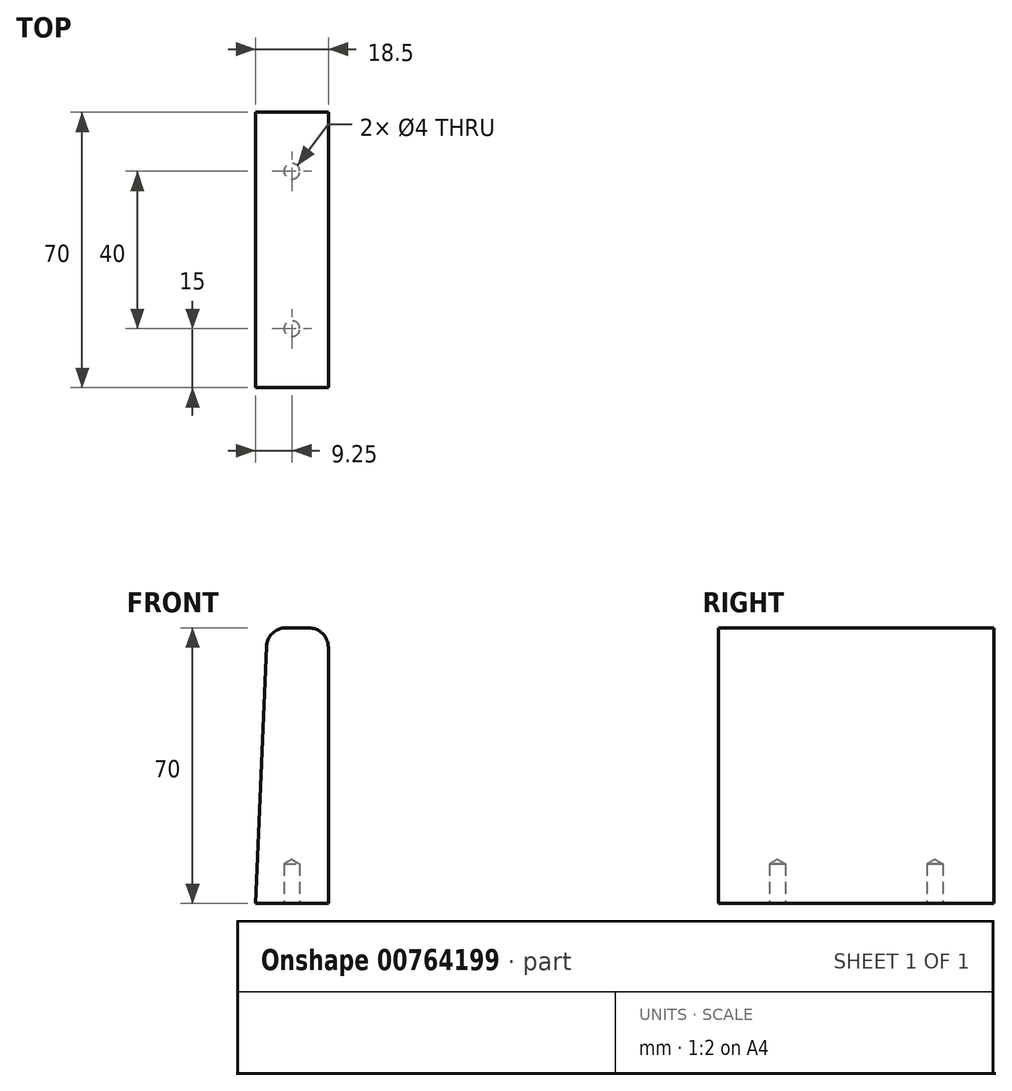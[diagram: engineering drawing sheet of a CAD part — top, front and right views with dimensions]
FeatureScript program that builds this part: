
annotation { "Feature Type Name" : "Feature", "Feature Type Description" : "" }
export const myFeature = defineFeature(function(context is Context, id is Id, definition is map)
    precondition{}
    {
        {
            var Q0;
            Q0=qCreatedBy(makeId("Front.planeOp"),FACE);
            var sketch = newSketch(context, id + "F0", { "sketchPlane" : qUnion([Q0])});
            skLineSegment(sketch, "E0", {"start": v(0, 0) * mm, "end": v(18.5, 0) * mm});
            skLineSegment(sketch, "E1", {"start": v(18.5, 0) * mm, "end": v(18.5, 70) * mm});
            skLineSegment(sketch, "E2", {"start": v(18.5, 70) * mm, "end": v(3, 70) * mm});
            skLineSegment(sketch, "E3", {"start": v(3, 70) * mm, "end": v(0, 0) * mm});
            skSolve(sketch);
        }
        {
            var Q0;
            Q0 = qSketchRegion(id + "F0", true);
            extrude(context, id + "F1", {"entities" : qUnion([Q0]), "depth" : 70 * mm, "offsetDistance" : 25 * mm});
        }
        {
            var Q0;
            Q0=makeQuery(id+"F1.opExtrude","SWEPT_EDGE",EDGE,{"disambiguationData":[OSD([sQuery(id+"F0.wireOp",EDGE,"E1"),sQuery(id+"F0.wireOp",EDGE,"E2")])]});
            var Q1;
            Q1=makeQuery(id+"F1.opExtrude","SWEPT_EDGE",EDGE,{"disambiguationData":[OSD([sQuery(id+"F0.wireOp",EDGE,"E2"),sQuery(id+"F0.wireOp",EDGE,"E3")])]});
            fillet(context, id + "F2", {"entities" : qUnion([Q0, Q1]), "tangentPropagation" : true, "radius" : 5 * mm, "defaultsChanged" : false, "vertexSettings" : [], "allowEdgeOverflow" : false});
        }
        {
            var Q0;
            Q0=makeQuery(id+"F1.opExtrude","SWEPT_FACE",FACE,{"disambiguationData":[OSD([sQuery(id+"F0.wireOp",EDGE,"E0")])]});
            var sketch = newSketch(context, id + "F3", { "sketchPlane" : qUnion([Q0])});
            skLineSegment(sketch, "E4", {"start": v(9.25, 55) * mm, "end": v(9.25, 15) * mm});
            skLineSegment(sketch, "E5", {"start": v(18.5, 35) * mm, "end": v(9.25, 35) * mm});
            skPoint(sketch, "E5.startSnap0", {"position": v(9.25, 35) * mm});
            skSolve(sketch);
        }
        {
            var Q0;
            Q0=sQuery(id+"F3.wireOp",VERTEX,"E4.start");
            var Q1;
            Q1=sQuery(id+"F3.wireOp",VERTEX,"E4.end");
            var Q2;
            Q2=makeQuery(id+"F1.opExtrude","SWEPT_BODY",BODY,{"disambiguationData":[OSD([sQuery(id+"F0.wireOp",EDGE,"E0"),sQuery(id+"F0.wireOp",EDGE,"E1"),sQuery(id+"F0.wireOp",EDGE,"E2"),sQuery(id+"F0.wireOp",EDGE,"E3")])]});
            hole(context, id + "F4", {"style" : HoleStyle.SIMPLE, "endStyle" : HoleEndStyle.BLIND, "holeDiameter" : 4 * mm, "majorDiameter" : 5 * mm, "holeDepth" : 10 * mm, "isTappedThrough" : true, "tappedDepth" : 12 * mm, "tapClearance" : 3, "locations" : qUnion([Q0, Q1]), "scope" : qUnion([Q2])});
        }
    });
